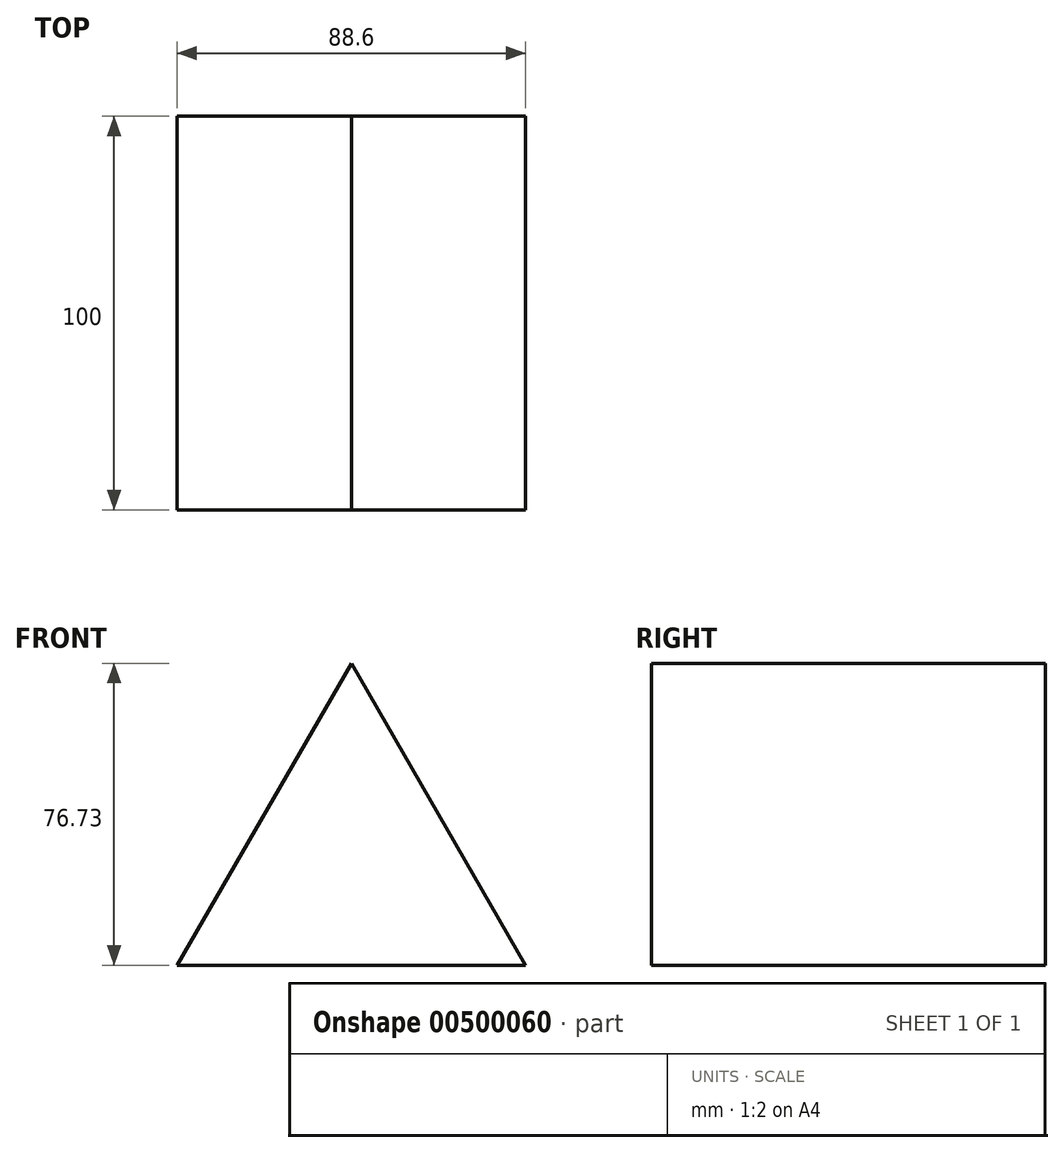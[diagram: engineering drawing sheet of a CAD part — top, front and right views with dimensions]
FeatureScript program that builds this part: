
annotation { "Feature Type Name" : "Feature", "Feature Type Description" : "" }
export const myFeature = defineFeature(function(context is Context, id is Id, definition is map)
    precondition{}
    {
        {
            var Q0;
            Q0=qCreatedBy(makeId("Front.planeOp"),FACE);
            var sketch = newSketch(context, id + "F0", { "sketchPlane" : qUnion([Q0])});
            skCircle(sketch, "E0.cCircle", {"center": v(0, 0) * mm, "radius": 51.15 * mm, "construction": true});
            skLineSegment(sketch, "E0.0", {"start": v(0, 51.15) * mm, "end": v(44.3, -25.58) * mm});
            skLineSegment(sketch, "E0.1", {"start": v(44.3, -25.58) * mm, "end": v(-44.3, -25.58) * mm});
            skLineSegment(sketch, "E0.2", {"start": v(-44.3, -25.58) * mm, "end": v(0, 51.15) * mm});
            skSolve(sketch);
        }
        {
            var Q0;
            Q0=makeQuery(id+"F0.imprint","IMPRINT",FACE,{"disambiguationData":[TD([[makeQuery(id+"F0.imprint","IMPRINT",EDGE,{"derivedFrom":sQuery(id+"F0.wireOp",EDGE,"E0.0")}),-1.0]])]});
            extrude(context, id + "F1", {"entities" : qUnion([Q0]), "depth" : 100 * mm, "symmetric" : true});
        }
    });
